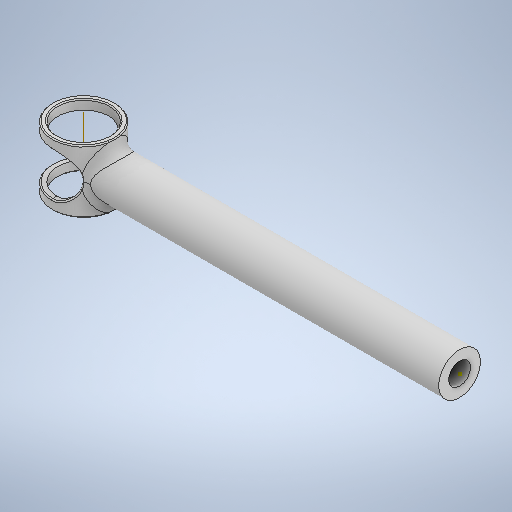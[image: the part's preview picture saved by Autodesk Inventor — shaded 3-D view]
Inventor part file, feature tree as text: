
AUTODESK INVENTOR PART (.ipt)
format: ipt  version: 2025.1 (Build 291241000, 241)  size: 410,624 bytes
history: native  units: mm
features: sketch x6, extrude x4, fillet x2, revolve x1, other x1
ambient origin geometry x8: Origin, YZ Plane, XZ Plane, XY Plane, X Axis, Y Axis, Z Axis, Center Point
bodies: Volumenkörper1 (feature_tree)
feature tree (14):
  revolve  "Umdrehung1"
  extrude  "Extrusion1"  Depth=4.0mm
  fillet  "Rundung1"  [1 undecoded]
  extrude  "Extrusion2"  TaperAngle=90.0deg  [1 undecoded]
  extrude  "Extrusion3"  Depth=12.0mm TaperAngle=0.0deg
  fillet  "Rundung2"  Radius=2.0mm
  sketch  "Skizze5"  dims[d12=4.15mm]
  extrude  "Extrusion4"  Depth=10.0mm TaperAngle=0.0deg
  other  "Arbeitsachse1"
  sketch  "Skizze1"  dims[d0=72.0mm d1=4.0mm d2=0.0mm]
  sketch  "Skizze2"  dims[d3=37.5mm d4=90.0deg]
  sketch  "Skizze3"  dims[d5=12.0mm d6=12.0mm d7=0.0mm d8=2.0mm]
  sketch  "Skizze4"  dims[d9=10.0mm d10=15.0mm d11=0.0mm]
  sketch  "Skizze6"  dims[d13=8.3mm d14=4.15mm d15=1.0mm d16=10.0mm d17=15.0mm d18=0.0mm d19=0.2mm d20=4.2mm d21=4.1mm d22=0.0mm]
note: 2 required parameter values undecoded (feature->parameter linkage not recoverable at this tier; creation-order binding heuristic only, values carry confidence <= 0.55)
